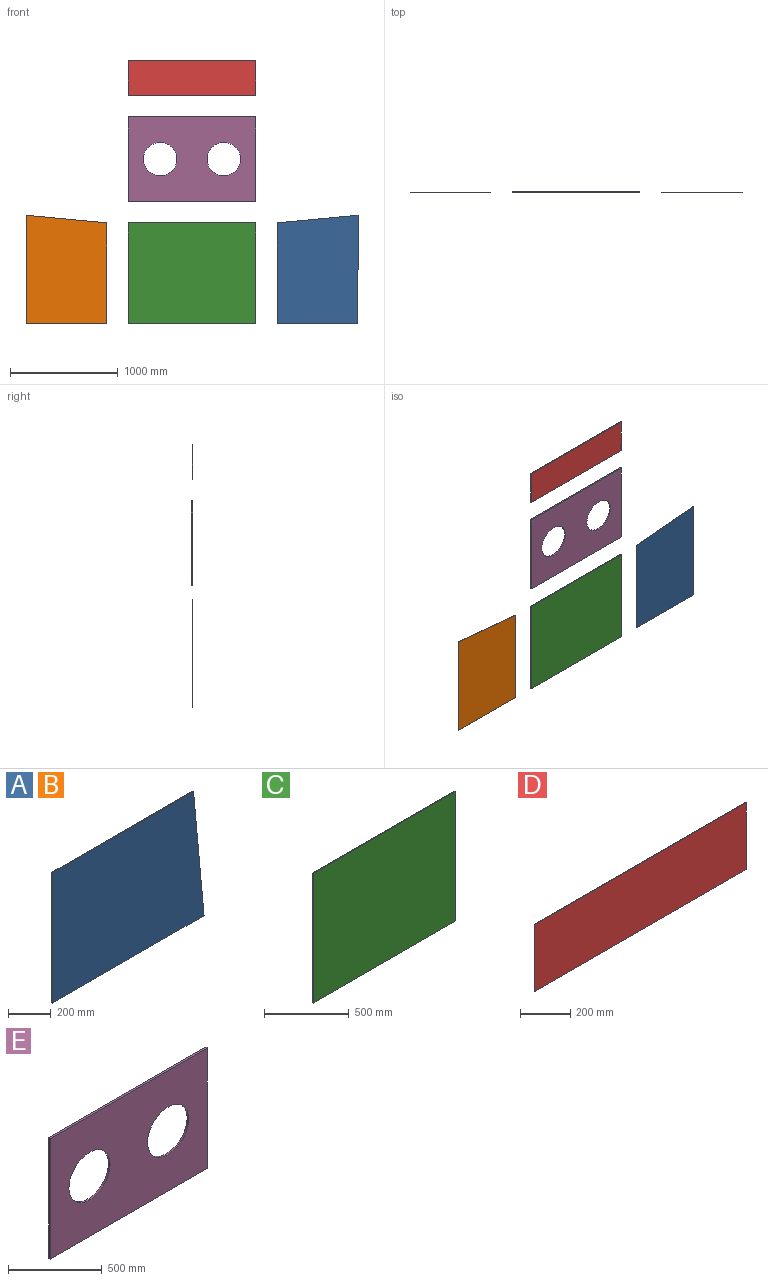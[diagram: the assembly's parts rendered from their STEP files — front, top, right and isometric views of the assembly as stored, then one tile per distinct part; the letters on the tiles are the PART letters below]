
ASSEMBLY  parts=5 mates=4
PART A: 6 faces, bbox 1006x5x750 mm
  f0: plane 936x5mm, normal (0,0,1), area 4680mm2, adj f1,f3,f4,f5
  f1: plane 750x5mm, normal (-1,0,0), area 3750mm2, adj f0,f2,f4,f5
  f2: plane 1006x5mm, normal (0,0,-1), area 5030mm2, adj f1,f3,f4,f5
  f3: plane 750x70mm, normal (1,0,0.09), area 3766.3mm2, adj f0,f2,f4,f5
  f4: plane 1006x750mm, normal (0,-1,0), area 728250mm2, adj f0,f1,f2,f3
  f5: plane 1006x750mm, normal (0,1,0), area 728250mm2, adj f0,f1,f2,f3
PART B: same geometry as A
PART C: 6 faces, bbox 1185x5x935 mm
  f0: plane 935x5mm, normal (-1,0,0), area 4675mm2, adj f1,f3,f4,f5
  f1: plane 1185x5mm, normal (0,0,-1), area 5925mm2, adj f0,f2,f4,f5
  f2: plane 935x5mm, normal (1,0,0), area 4675mm2, adj f1,f3,f4,f5
  f3: plane 1185x5mm, normal (0,0,1), area 5925mm2, adj f0,f2,f4,f5
  f4: plane 1185x935mm, normal (0,-1,0), area 1107975mm2, adj f0,f1,f2,f3
  f5: plane 1185x935mm, normal (0,1,0), area 1107975mm2, adj f0,f1,f2,f3
PART D: 6 faces, bbox 1185x5x325 mm
  f0: plane 325x5mm, normal (-1,0,0), area 1625mm2, adj f1,f3,f4,f5
  f1: plane 1185x5mm, normal (0,0,-1), area 5925mm2, adj f0,f2,f4,f5
  f2: plane 325x5mm, normal (1,0,0), area 1625mm2, adj f1,f3,f4,f5
  f3: plane 1185x5mm, normal (0,0,1), area 5925mm2, adj f0,f2,f4,f5
  f4: plane 1185x325mm, normal (0,-1,0), area 385125mm2, adj f0,f1,f2,f3
  f5: plane 1185x325mm, normal (0,1,0), area 385125mm2, adj f0,f1,f2,f3
PART E: 8 faces, bbox 1185x12x785 mm
  f0: plane 785x12mm, normal (-1,0,0), area 9420mm2, adj f1,f4,f6,f7
  f1: plane 1185x12mm, normal (0,0,-1), area 14220mm2, adj f0,f2,f6,f7
  f2: plane 785x12mm, normal (1,0,0), area 9420mm2, adj f1,f4,f6,f7
  f3: cylinder r=155mm len=310mm, axis (0,1,0), area 11686.7mm2, adj f6,f7
  f4: plane 1185x12mm, normal (0,0,1), area 14220mm2, adj f0,f2,f6,f7
  f5: cylinder r=155mm len=310mm, axis (0,1,0), area 11686.7mm2, adj f6,f7
  f6: plane 1185x785mm, normal (0,-1,0), area 779271.5mm2, adj f0,f1,f2,f3,f4,f5
  f7: plane 1185x785mm, normal (0,1,0), area 779271.5mm2, adj f0,f1,f2,f3,f4,f5
PLACE A rot(axis=(0,-1,0),90deg) t=(2135,5,0)mm
PLACE B rot(axis=(0.71,0,0.71),180deg) t=(-950,0,0)mm
PLACE C t=(0,5,0)mm
PLACE D t=(0,5,2120)mm
PLACE E t=(0,12,1135)mm
MATE fastened D.f4 <-> E.f6  axis (0,-1,0) through (0,0,2120)mm
MATE fastened C.f4 <-> B.f5  axis (0,-1,0) through (0,0,0)mm
MATE fastened A.f4 <-> C.f4  axis (0,-1,0) through (1385,0,0)mm
MATE fastened E.f6 <-> C.f4  axis (0,-1,0) through (0,0,1135)mm
